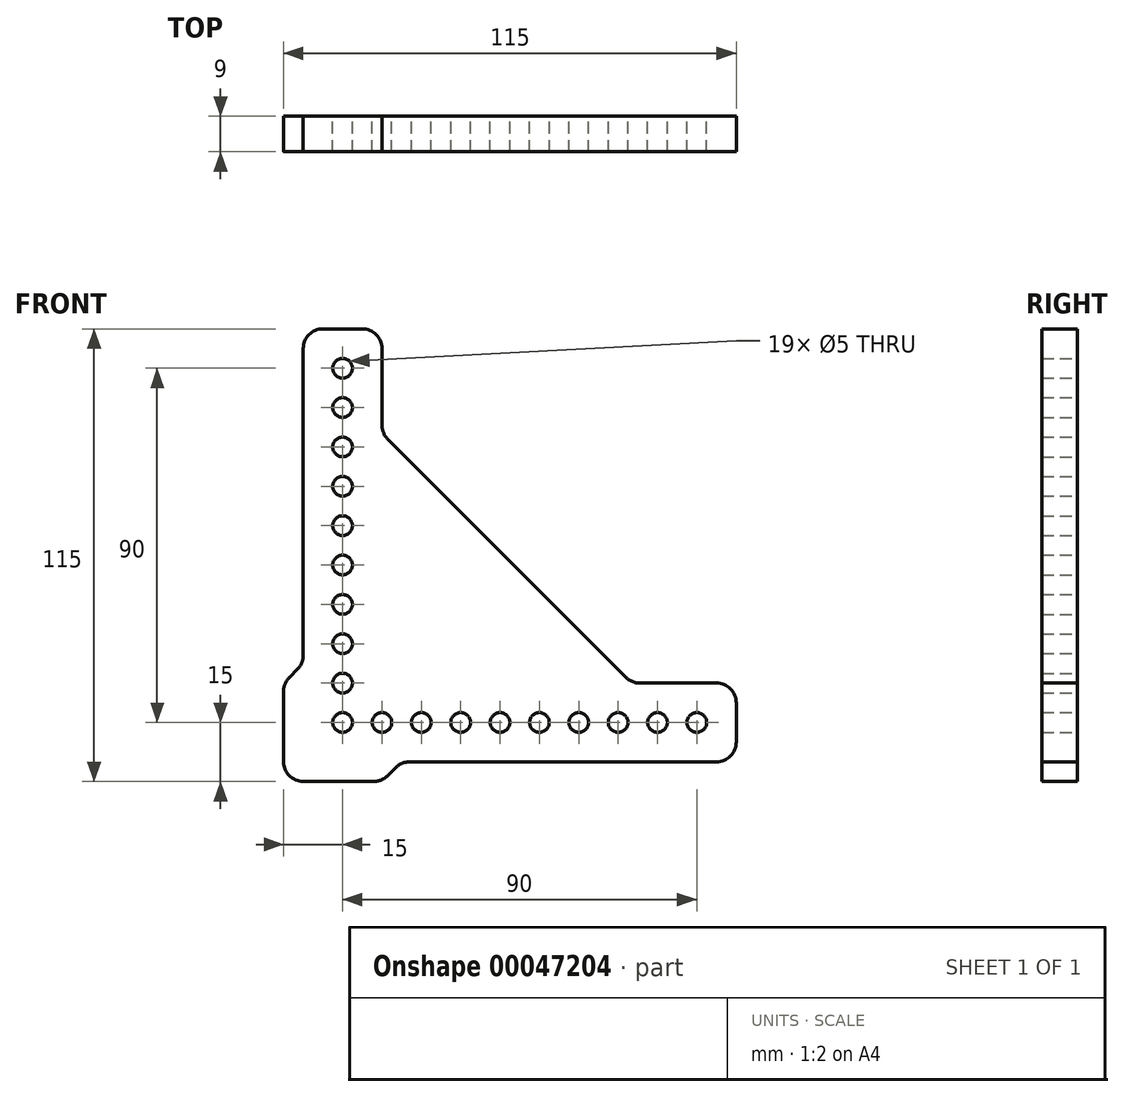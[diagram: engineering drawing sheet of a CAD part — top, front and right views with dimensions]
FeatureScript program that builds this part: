
annotation { "Feature Type Name" : "Feature", "Feature Type Description" : "" }
export const myFeature = defineFeature(function(context is Context, id is Id, definition is map)
    precondition{}
    {
        {
            var Q0;
            Q0=qCreatedBy(makeId("Front.planeOp"),FACE);
            var sketch = newSketch(context, id + "F0", { "sketchPlane" : qUnion([Q0])});
            skLineSegment(sketch, "E0", {"start": v(0, 105) * mm, "end": v(0, 27.07) * mm});
            skLineSegment(sketch, "E1", {"start": v(27.07, 0) * mm, "end": v(105, 0) * mm});
            skLineSegment(sketch, "E2", {"start": v(110, 5) * mm, "end": v(110, 15) * mm});
            skLineSegment(sketch, "E3", {"start": v(105, 20) * mm, "end": v(85.52, 20) * mm});
            skLineSegment(sketch, "E4", {"start": v(81.99, 21.46) * mm, "end": v(21.46, 81.99) * mm});
            skLineSegment(sketch, "E5", {"start": v(20, 85.52) * mm, "end": v(20, 105) * mm});
            skLineSegment(sketch, "E6", {"start": v(15, 110) * mm, "end": v(5, 110) * mm});
            skLineSegment(sketch, "E7", {"start": v(10, 110) * mm, "end": v(10, 0) * mm, "construction": true});
            skLineSegment(sketch, "E8", {"start": v(110, 10) * mm, "end": v(0, 10) * mm, "construction": true});
            skCircle(sketch, "E9", {"center": v(10, 10) * mm, "radius": 2.5 * mm});
            skCircle(sketch, "E10.1.0.0", {"center": v(20, 10) * mm, "radius": 2.5 * mm});
            skCircle(sketch, "E10.2.0.0", {"center": v(30, 10) * mm, "radius": 2.5 * mm});
            skCircle(sketch, "E10.3.0.0", {"center": v(40, 10) * mm, "radius": 2.5 * mm});
            skCircle(sketch, "E10.4.0.0", {"center": v(50, 10) * mm, "radius": 2.5 * mm});
            skCircle(sketch, "E10.5.0.0", {"center": v(60, 10) * mm, "radius": 2.5 * mm});
            skCircle(sketch, "E10.6.0.0", {"center": v(70, 10) * mm, "radius": 2.5 * mm});
            skLineSegment(sketch, "E10.direction1", {"start": v(10, 10) * mm, "end": v(20, 10) * mm, "construction": true});
            skCircle(sketch, "E11.0.1.0", {"center": v(10, 20) * mm, "radius": 2.5 * mm});
            skCircle(sketch, "E11.0.2.0", {"center": v(10, 30) * mm, "radius": 2.5 * mm});
            skCircle(sketch, "E11.0.3.0", {"center": v(10, 40) * mm, "radius": 2.5 * mm});
            skCircle(sketch, "E11.0.4.0", {"center": v(10, 50) * mm, "radius": 2.5 * mm});
            skCircle(sketch, "E11.0.5.0", {"center": v(10, 60) * mm, "radius": 2.5 * mm});
            skCircle(sketch, "E11.0.6.0", {"center": v(10, 70) * mm, "radius": 2.5 * mm});
            skCircle(sketch, "E11.0.7.0", {"center": v(10, 80) * mm, "radius": 2.5 * mm});
            skLineSegment(sketch, "E11.direction1", {"start": v(10, 10) * mm, "end": v(35, 10) * mm, "construction": true});
            skLineSegment(sketch, "E11.direction2", {"start": v(10, 10) * mm, "end": v(10, 20) * mm, "construction": true});
            skCircle(sketch, "E12.0.7.0", {"center": v(80, 10) * mm, "radius": 2.5 * mm});
            skCircle(sketch, "E13.0.0.8", {"center": v(10, 90) * mm, "radius": 2.5 * mm});
            skCircle(sketch, "E13.0.0.9", {"center": v(10, 100) * mm, "radius": 2.5 * mm});
            skCircle(sketch, "E14.0.8.0", {"center": v(90, 10) * mm, "radius": 2.5 * mm});
            skCircle(sketch, "E14.0.9.0", {"center": v(100, 10) * mm, "radius": 2.5 * mm});
            skLineSegment(sketch, "E15", {"start": v(0, -5) * mm, "end": v(0, -5) * mm});
            skLineSegment(sketch, "E16", {"start": v(-5, 0) * mm, "end": v(-5, 0) * mm});
            skLineSegment(sketch, "E17", {"start": v(-5, 0) * mm, "end": v(-5, 17.93) * mm});
            skLineSegment(sketch, "E18", {"start": v(0, -5) * mm, "end": v(17.93, -5) * mm});
            skLineSegment(sketch, "E19", {"start": v(-3.54, 21.46) * mm, "end": v(-1.46, 23.54) * mm});
            skLineSegment(sketch, "E20", {"start": v(21.46, -3.54) * mm, "end": v(23.54, -1.46) * mm});
            skPoint(sketch, "E21.newPointA", {"position": v(0, 0) * mm});
            skArc(sketch, "E21.filletArc", {"start": v(-1.46, 23.54) * mm, "mid": v(-0.38, 25.16) * mm, "end": v(0, 27.07) * mm});
            skPoint(sketch, "E22.visualSharp", {"position": v(-5, 20) * mm});
            skArc(sketch, "E22.filletArc", {"start": v(-3.54, 21.46) * mm, "mid": v(-4.62, 19.84) * mm, "end": v(-5, 17.93) * mm});
            skPoint(sketch, "E23.visualSharp", {"position": v(-5, -5) * mm});
            skArc(sketch, "E23.filletArc", {"start": v(-5, 0) * mm, "mid": v(-3.54, -3.54) * mm, "end": v(0, -5) * mm});
            skPoint(sketch, "E24.visualSharp", {"position": v(20, -5) * mm});
            skArc(sketch, "E24.filletArc", {"start": v(17.93, -5) * mm, "mid": v(19.84, -4.62) * mm, "end": v(21.46, -3.54) * mm});
            skArc(sketch, "E25.filletArc", {"start": v(27.07, 0) * mm, "mid": v(25.16, -0.38) * mm, "end": v(23.54, -1.46) * mm});
            skPoint(sketch, "E26.visualSharp", {"position": v(83.45, 20) * mm});
            skArc(sketch, "E26.filletArc", {"start": v(81.99, 21.46) * mm, "mid": v(83.61, 20.38) * mm, "end": v(85.52, 20) * mm});
            skPoint(sketch, "E27.visualSharp", {"position": v(20, 83.45) * mm});
            skArc(sketch, "E27.filletArc", {"start": v(20, 85.52) * mm, "mid": v(20.38, 83.61) * mm, "end": v(21.46, 81.99) * mm});
            skPoint(sketch, "E28.visualSharp", {"position": v(20, 110) * mm});
            skArc(sketch, "E28.filletArc", {"start": v(20, 105) * mm, "mid": v(18.54, 108.54) * mm, "end": v(15, 110) * mm});
            skPoint(sketch, "E29.visualSharp", {"position": v(0, 110) * mm});
            skArc(sketch, "E29.filletArc", {"start": v(5, 110) * mm, "mid": v(1.46, 108.54) * mm, "end": v(0, 105) * mm});
            skPoint(sketch, "E30.visualSharp", {"position": v(110, 20) * mm});
            skArc(sketch, "E30.filletArc", {"start": v(110, 15) * mm, "mid": v(108.54, 18.54) * mm, "end": v(105, 20) * mm});
            skPoint(sketch, "E31.visualSharp", {"position": v(110, 0) * mm});
            skArc(sketch, "E31.filletArc", {"start": v(105, 0) * mm, "mid": v(108.54, 1.46) * mm, "end": v(110, 5) * mm});
            skSolve(sketch);
        }
        {
            var Q0;
            Q0=makeQuery(id+"F0.imprint","IMPRINT",FACE,{"disambiguationData":[TD([[makeQuery(id+"F0.imprint","IMPRINT",EDGE,{"derivedFrom":sQuery(id+"F0.wireOp",EDGE,"E0")}),1.0]])]});
            extrude(context, id + "F1", {"entities" : qUnion([Q0]), "depth" : 9 * mm});
        }
    });
